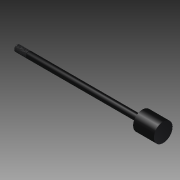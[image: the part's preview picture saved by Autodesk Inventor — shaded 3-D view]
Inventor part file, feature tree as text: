
AUTODESK INVENTOR PART (.ipt)
format: ipt  version: 2011 SP1 (Build 150282100, 282)  size: 120,832 bytes
history: native  units: in
note: dims shown in document units (in); Inventor stores cm internally (conversion verified against a paired STEP export)
features: other x70, revolve x3, sketch x3, thread x1
ambient origin geometry x8: Origin, YZ Plane, XZ Plane, XY Plane, X Axis, Y Axis, Z Axis, Center Point
bodies: Solid1 (feature_tree)
feature tree (77):
  revolve  "Revolution1"  Angle=360.0deg
  revolve  "Revolution2"  Angle=360.0deg
  thread  "Thread1"  [1 undecoded]
  revolve  "Revolution3"  [1 undecoded]
  other  "dia1_XY"
  other  "dia1_YZ"
  other  "dia1_ZX"
  other  "dia1_X"
  other  "dia1_Y"
  other  "dia1_Z"
  other  "dia1_Center"
  other  "dia12_XY"
  other  "dia12_YZ"
  other  "dia12_ZX"
  other  "dia12_X"
  other  "dia12_Y"
  other  "dia12_Z"
  other  "dia12_Center"
  other  "dia2_XY"
  other  "dia2_YZ"
  other  "dia2_ZX"
  other  "dia2_X"
  other  "dia2_Y"
  other  "dia2_Z"
  other  "dia2_Center"
  other  "dia22_XY"
  other  "dia22_YZ"
  other  "dia22_ZX"
  other  "dia22_X"
  other  "dia22_Y"
  other  "dia22_Z"
  other  "dia22_Center"
  other  "rl1_XY"
  other  "rl1_YZ"
  other  "rl1_ZX"
  other  "rl1_X"
  other  "rl1_Y"
  other  "rl1_Z"
  other  "rl1_Center"
  other  "rl2_XY"
  other  "rl2_YZ"
  other  "rl2_ZX"
  other  "rl2_X"
  other  "rl2_Y"
  other  "rl2_Z"
  other  "rl2_Center"
  other  "rod_cp_XY"
  other  "rod_cp_YZ"
  other  "rod_cp_ZX"
  other  "rod_cp_X"
  other  "rod_cp_Y"
  other  "rod_cp_Z"
  other  "rod_cp_Center"
  other  "thd1_XY"
  other  "thd1_YZ"
  other  "thd1_ZX"
  other  "thd1_X"
  other  "thd1_Y"
  other  "thd1_Z"
  other  "thd1_Center"
  other  "thd2_XY"
  other  "thd2_YZ"
  other  "thd2_ZX"
  other  "thd2_X"
  other  "thd2_Y"
  other  "thd2_Z"
  other  "thd2_Center"
  other  "to_rod_clevis_XY"
  other  "to_rod_clevis_YZ"
  other  "to_rod_clevis_ZX"
  other  "to_rod_clevis_X"
  other  "to_rod_clevis_Y"
  other  "to_rod_clevis_Z"
  other  "to_rod_clevis_Center"
  sketch  "Sketch_1"  dims[d0=360.0deg d1=360.0deg]
  sketch  "Sketch_3"  dims[d2=0.4787in d3=0.0in d4=360.0deg d5=0.0in d6=0.0in d7=0.0in]
  sketch  "Sketch_30"
note: 2 required parameter values undecoded (feature->parameter linkage not recoverable at this tier; creation-order binding heuristic only, values carry confidence <= 0.55)
